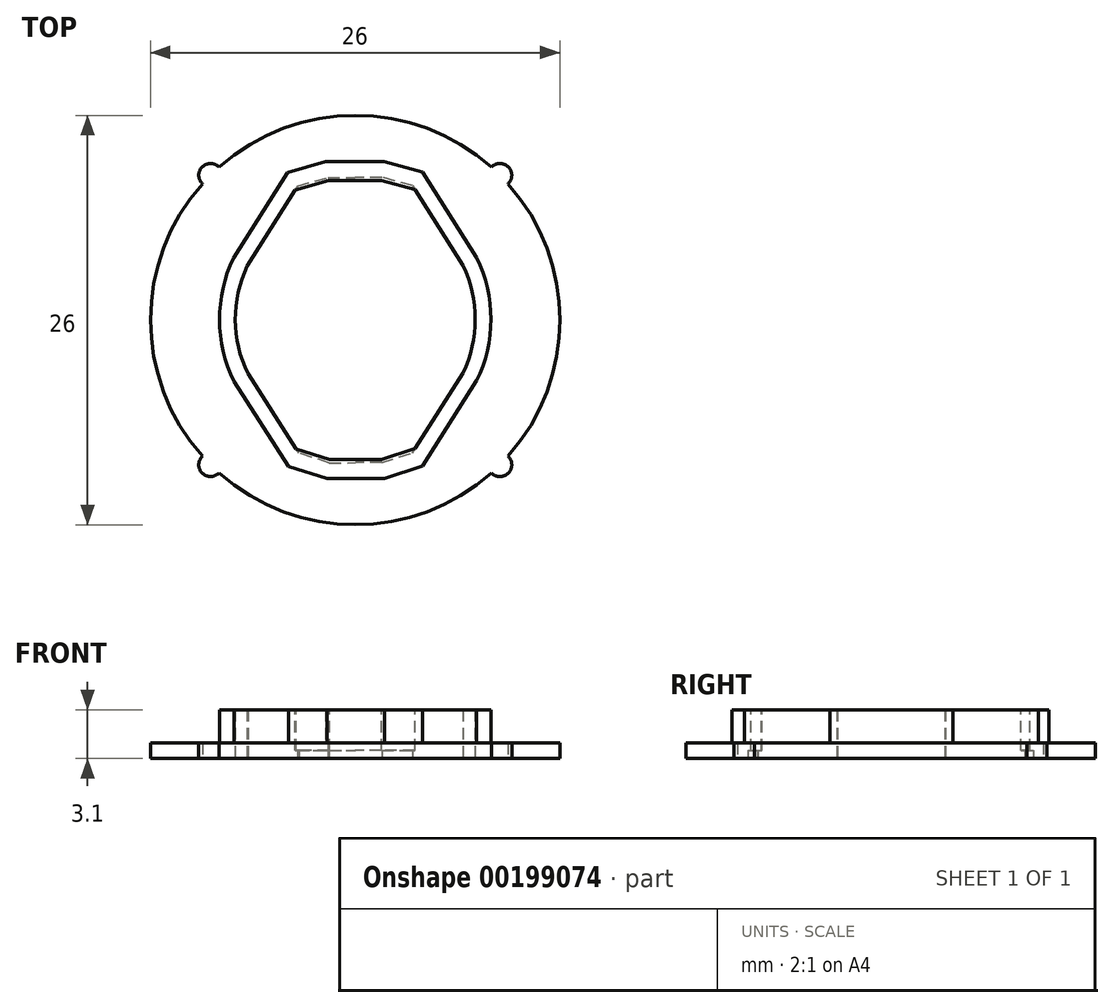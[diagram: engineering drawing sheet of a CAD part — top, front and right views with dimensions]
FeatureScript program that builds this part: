
annotation { "Feature Type Name" : "Feature", "Feature Type Description" : "" }
export const myFeature = defineFeature(function(context is Context, id is Id, definition is map)
    precondition{}
    {
        {
            var Q0;
            Q0=qCreatedBy(makeId("Top.planeOp"),FACE);
            var sketch = newSketch(context, id + "F0", { "sketchPlane" : qUnion([Q0])});
            skLineSegment(sketch, "E0", {"start": v(-52.92, -44.13) * mm, "end": v(-52.88, -62.26) * mm, "construction": true});
            skCircle(sketch, "E1", {"center": v(-52.9, -53.2) * mm, "radius": 13 * mm});
            skLineSegment(sketch, "E2", {"start": v(-49.27, -44.66) * mm, "end": v(-46.06, -49.73) * mm});
            skLineSegment(sketch, "E3", {"start": v(-49.27, -44.66) * mm, "end": v(-51.2, -44.13) * mm});
            skLineSegment(sketch, "E4", {"start": v(-51.2, -44.13) * mm, "end": v(-52.92, -44.13) * mm});
            skLineSegment(sketch, "E5", {"start": v(-52.92, -44.13) * mm, "end": v(-52.88, -62.26) * mm});
            skLineSegment(sketch, "E6", {"start": v(-51.2, -62.26) * mm, "end": v(-49.27, -61.63) * mm});
            skLineSegment(sketch, "E7", {"start": v(-49.27, -61.63) * mm, "end": v(-46.06, -56.57) * mm});
            skArc(sketch, "E8", {"start": v(-46.06, -56.57) * mm, "mid": v(-45.28, -53.15) * mm, "end": v(-46.06, -49.73) * mm});
            skLineSegment(sketch, "E9.MirrorCS", {"start": v(-54.64, -44.14) * mm, "end": v(-52.92, -44.13) * mm});
            skLineSegment(sketch, "E10.MirrorCS", {"start": v(-56.56, -44.68) * mm, "end": v(-54.64, -44.14) * mm});
            skLineSegment(sketch, "E11.MirrorCS", {"start": v(-56.56, -44.68) * mm, "end": v(-59.76, -49.76) * mm});
            skArc(sketch, "E12.MirrorCS", {"start": v(-59.72, -56.6) * mm, "mid": v(-60.52, -53.18) * mm, "end": v(-59.76, -49.76) * mm});
            skLineSegment(sketch, "E13.MirrorCS", {"start": v(-56.48, -61.65) * mm, "end": v(-59.72, -56.6) * mm});
            skLineSegment(sketch, "E14.MirrorCS", {"start": v(-54.55, -62.27) * mm, "end": v(-56.48, -61.65) * mm});
            skLineSegment(sketch, "E15", {"start": v(-54.55, -62.27) * mm, "end": v(-52.88, -62.26) * mm});
            skLineSegment(sketch, "E16", {"start": v(-51.2, -62.26) * mm, "end": v(-52.88, -62.26) * mm});
            skLineSegment(sketch, "E17.0", {"start": v(-48.64, -43.8) * mm, "end": v(-51.07, -43.13) * mm});
            skLineSegment(sketch, "E17.1", {"start": v(-51.07, -43.13) * mm, "end": v(-52.92, -43.13) * mm});
            skLineSegment(sketch, "E17.2", {"start": v(-54.78, -43.14) * mm, "end": v(-52.92, -43.13) * mm});
            skLineSegment(sketch, "E17.3", {"start": v(-51.04, -63.26) * mm, "end": v(-52.87, -63.26) * mm});
            skLineSegment(sketch, "E17.4", {"start": v(-51.04, -63.26) * mm, "end": v(-48.62, -62.47) * mm});
            skLineSegment(sketch, "E17.5", {"start": v(-48.62, -62.47) * mm, "end": v(-45.18, -57.06) * mm});
            skArc(sketch, "E17.6", {"start": v(-45.18, -57.06) * mm, "mid": v(-44.28, -53.15) * mm, "end": v(-45.18, -49.24) * mm});
            skLineSegment(sketch, "E17.7", {"start": v(-54.7, -63.27) * mm, "end": v(-52.87, -63.26) * mm});
            skLineSegment(sketch, "E17.8", {"start": v(-54.7, -63.27) * mm, "end": v(-57.13, -62.5) * mm});
            skLineSegment(sketch, "E17.9", {"start": v(-57.13, -62.5) * mm, "end": v(-60.6, -57.1) * mm});
            skLineSegment(sketch, "E17.10", {"start": v(-48.64, -43.8) * mm, "end": v(-45.18, -49.24) * mm});
            skArc(sketch, "E17.11", {"start": v(-60.6, -57.1) * mm, "mid": v(-61.52, -53.19) * mm, "end": v(-60.63, -49.28) * mm});
            skLineSegment(sketch, "E17.12", {"start": v(-57.2, -43.82) * mm, "end": v(-60.63, -49.28) * mm});
            skLineSegment(sketch, "E17.13", {"start": v(-57.2, -43.82) * mm, "end": v(-54.78, -43.14) * mm});
            skLineSegment(sketch, "E18.bottom", {"start": v(-43.7, -44) * mm, "end": v(-62.1, -44) * mm, "construction": true});
            skLineSegment(sketch, "E18.top", {"start": v(-43.7, -62.4) * mm, "end": v(-62.1, -62.4) * mm, "construction": true});
            skLineSegment(sketch, "E18.left", {"start": v(-43.7, -44) * mm, "end": v(-43.7, -62.4) * mm, "construction": true});
            skLineSegment(sketch, "E18.right", {"start": v(-62.1, -44) * mm, "end": v(-62.1, -62.4) * mm, "construction": true});
            skCircle(sketch, "E19", {"center": v(-43.7, -44) * mm, "radius": 0.5 * mm});
            skCircle(sketch, "E20", {"center": v(-62.1, -44) * mm, "radius": 0.5 * mm});
            skCircle(sketch, "E21", {"center": v(-43.7, -62.4) * mm, "radius": 0.5 * mm});
            skCircle(sketch, "E22", {"center": v(-62.1, -62.4) * mm, "radius": 0.5 * mm});
            skCircle(sketch, "E23", {"center": v(-62.1, -44) * mm, "radius": 0.75 * mm});
            skCircle(sketch, "E24", {"center": v(-43.7, -44) * mm, "radius": 0.75 * mm});
            skCircle(sketch, "E25", {"center": v(-43.7, -62.4) * mm, "radius": 0.75 * mm});
            skCircle(sketch, "E26", {"center": v(-62.1, -62.4) * mm, "radius": 0.75 * mm});
            skSolve(sketch);
        }
        {
            var Q0;
            Q0=makeQuery(id+"F0.imprint","IMPRINT",FACE,{"disambiguationData":[TD([[makeQuery(id+"F0.imprint","IMPRINT",EDGE,{"derivedFrom":sQuery(id+"F0.wireOp",EDGE,"E2")}),1.0]])]});
            var Q1;
            Q1=sQuery(id+"F0.wireOp",EDGE,"E17.11");
            var Q2;
            Q2=sQuery(id+"F0.wireOp",EDGE,"E12.MirrorCS");
            extrude(context, id + "F1", {"entities" : qUnion([Q0]), "surfaceEntities" : qUnion([Q1, Q2]), "depth" : 3.1 * mm});
        }
        {
            var Q0;
            Q0=makeQuery(id+"F1.opExtrude","CAP_FACE",FACE,{"disambiguationData":[OSD([sQuery(id+"F0.wireOp",EDGE,"E2"),sQuery(id+"F0.wireOp",EDGE,"E3"),sQuery(id+"F0.wireOp",EDGE,"E4"),sQuery(id+"F0.wireOp",EDGE,"E6"),sQuery(id+"F0.wireOp",EDGE,"E7"),sQuery(id+"F0.wireOp",EDGE,"E8"),sQuery(id+"F0.wireOp",EDGE,"E9.MirrorCS"),sQuery(id+"F0.wireOp",EDGE,"E10.MirrorCS"),sQuery(id+"F0.wireOp",EDGE,"E11.MirrorCS"),sQuery(id+"F0.wireOp",EDGE,"E12.MirrorCS"),sQuery(id+"F0.wireOp",EDGE,"E13.MirrorCS"),sQuery(id+"F0.wireOp",EDGE,"E14.MirrorCS"),sQuery(id+"F0.wireOp",EDGE,"E15"),sQuery(id+"F0.wireOp",EDGE,"E16"),sQuery(id+"F0.wireOp",EDGE,"E17.0"),sQuery(id+"F0.wireOp",EDGE,"E17.1"),sQuery(id+"F0.wireOp",EDGE,"E17.2"),sQuery(id+"F0.wireOp",EDGE,"E17.3"),sQuery(id+"F0.wireOp",EDGE,"E17.4"),sQuery(id+"F0.wireOp",EDGE,"E17.5"),sQuery(id+"F0.wireOp",EDGE,"E17.6"),sQuery(id+"F0.wireOp",EDGE,"E17.7"),sQuery(id+"F0.wireOp",EDGE,"E17.8"),sQuery(id+"F0.wireOp",EDGE,"E17.9"),sQuery(id+"F0.wireOp",EDGE,"E17.10"),sQuery(id+"F0.wireOp",EDGE,"E17.11"),sQuery(id+"F0.wireOp",EDGE,"E17.12"),sQuery(id+"F0.wireOp",EDGE,"E17.13")])],"isStart":true});
            var sketch = newSketch(context, id + "F2", { "sketchPlane" : qUnion([Q0])});
            skLineSegment(sketch, "E27", {"start": v(-52.92, 44.13) * mm, "end": v(-52.88, 62.26) * mm, "construction": true});
            skCircle(sketch, "E28", {"center": v(-52.9, 53.2) * mm, "radius": 13 * mm});
            skLineSegment(sketch, "E29.bottom", {"start": v(-43.7, 62.4) * mm, "end": v(-62.1, 62.4) * mm, "construction": true});
            skLineSegment(sketch, "E29.top", {"start": v(-43.7, 44) * mm, "end": v(-62.1, 44) * mm, "construction": true});
            skLineSegment(sketch, "E29.left", {"start": v(-43.7, 62.4) * mm, "end": v(-43.7, 44) * mm, "construction": true});
            skLineSegment(sketch, "E29.right", {"start": v(-62.1, 62.4) * mm, "end": v(-62.1, 44) * mm, "construction": true});
            skCircle(sketch, "E30", {"center": v(-43.7, 62.4) * mm, "radius": 0.5 * mm});
            skCircle(sketch, "E31", {"center": v(-62.1, 62.4) * mm, "radius": 0.5 * mm});
            skCircle(sketch, "E32", {"center": v(-43.7, 44) * mm, "radius": 0.5 * mm});
            skCircle(sketch, "E33", {"center": v(-62.1, 44) * mm, "radius": 0.5 * mm});
            skCircle(sketch, "E34", {"center": v(-43.7, 44) * mm, "radius": 0.75 * mm});
            skCircle(sketch, "E35", {"center": v(-62.1, 44) * mm, "radius": 0.75 * mm});
            skCircle(sketch, "E36", {"center": v(-62.1, 62.4) * mm, "radius": 0.75 * mm});
            skCircle(sketch, "E37", {"center": v(-43.7, 62.4) * mm, "radius": 0.75 * mm});
            skSolve(sketch);
        }
        {
            var Q0;
            {var subQ0=sQuery(id+"F2.wireOp",EDGE,"E37");var subQ1=sQuery(id+"F2.wireOp",EDGE,"E28");var subQ2=makeQuery(id+"F2.imprint","INTERSECT",VERTEX,{"disambiguationData":[OD(0.0)],"derivedFrom":[subQ1,subQ0]});Q0=makeQuery(id+"F2.imprint","IMPRINT",FACE,{"disambiguationData":[TD([[makeQuery(id+"F2.imprint","IMPRINT",EDGE,{"disambiguationData":[TD([[subQ2,-1.0]])],"derivedFrom":subQ1}),-1.0]])]});}
            var Q1;
            {var subQ0=sQuery(id+"F2.wireOp",EDGE,"E30");var subQ1=sQuery(id+"F2.wireOp",EDGE,"E28");var subQ2=makeQuery(id+"F2.imprint","INTERSECT",VERTEX,{"disambiguationData":[OD(0.0)],"derivedFrom":[subQ1,subQ0]});Q1=makeQuery(id+"F2.imprint","IMPRINT",FACE,{"disambiguationData":[TD([[makeQuery(id+"F2.imprint","IMPRINT",EDGE,{"disambiguationData":[TD([[subQ2,-1.0]])],"derivedFrom":subQ1}),-1.0]])]});}
            var Q2;
            {var subQ0=sQuery(id+"F2.wireOp",EDGE,"E30");var subQ1=sQuery(id+"F2.wireOp",EDGE,"E28");var subQ2=makeQuery(id+"F2.imprint","INTERSECT",VERTEX,{"disambiguationData":[OD(0.0)],"derivedFrom":[subQ1,subQ0]});Q2=makeQuery(id+"F2.imprint","IMPRINT",FACE,{"disambiguationData":[TD([[makeQuery(id+"F2.imprint","IMPRINT",EDGE,{"disambiguationData":[TD([[subQ2,-1.0]])],"derivedFrom":subQ1}),1.0]])]});}
            var Q3;
            Q3=makeQuery(id+"F2.imprint","IMPRINT",FACE,{"disambiguationData":[TD([[makeQuery(id+"F2.imprint","IMPRINT",EDGE,{"derivedFrom":makeQuery(id+"F1.opExtrude","CAP_EDGE",EDGE,{"disambiguationData":[OSD([sQuery(id+"F0.wireOp",EDGE,"E17.0")])],"isStart":true})}),1.0]])]});
            var Q4;
            {var subQ0=sQuery(id+"F2.wireOp",EDGE,"E37");var subQ1=sQuery(id+"F2.wireOp",EDGE,"E28");var subQ2=makeQuery(id+"F2.imprint","INTERSECT",VERTEX,{"disambiguationData":[OD(0.0)],"derivedFrom":[subQ1,subQ0]});Q4=makeQuery(id+"F2.imprint","IMPRINT",FACE,{"disambiguationData":[TD([[makeQuery(id+"F2.imprint","IMPRINT",EDGE,{"disambiguationData":[TD([[subQ2,-1.0]])],"derivedFrom":subQ1}),1.0]])]});}
            var Q5;
            {var subQ0=sQuery(id+"F2.wireOp",EDGE,"E36");var subQ1=sQuery(id+"F2.wireOp",EDGE,"E28");var subQ2=makeQuery(id+"F2.imprint","INTERSECT",VERTEX,{"disambiguationData":[OD(0.0)],"derivedFrom":[subQ1,subQ0]});Q5=makeQuery(id+"F2.imprint","IMPRINT",FACE,{"disambiguationData":[TD([[makeQuery(id+"F2.imprint","IMPRINT",EDGE,{"disambiguationData":[TD([[subQ2,-1.0]])],"derivedFrom":subQ1}),-1.0]])]});}
            var Q6;
            {var subQ0=sQuery(id+"F2.wireOp",EDGE,"E36");var subQ1=sQuery(id+"F2.wireOp",EDGE,"E28");var subQ2=makeQuery(id+"F2.imprint","INTERSECT",VERTEX,{"disambiguationData":[OD(0.0)],"derivedFrom":[subQ1,subQ0]});Q6=makeQuery(id+"F2.imprint","IMPRINT",FACE,{"disambiguationData":[TD([[makeQuery(id+"F2.imprint","IMPRINT",EDGE,{"disambiguationData":[TD([[subQ2,-1.0]])],"derivedFrom":subQ1}),1.0]])]});}
            var Q7;
            {var subQ0=sQuery(id+"F2.wireOp",EDGE,"E31");var subQ1=sQuery(id+"F2.wireOp",EDGE,"E28");var subQ2=makeQuery(id+"F2.imprint","INTERSECT",VERTEX,{"disambiguationData":[OD(0.0)],"derivedFrom":[subQ1,subQ0]});Q7=makeQuery(id+"F2.imprint","IMPRINT",FACE,{"disambiguationData":[TD([[makeQuery(id+"F2.imprint","IMPRINT",EDGE,{"disambiguationData":[TD([[subQ2,-1.0]])],"derivedFrom":subQ1}),-1.0]])]});}
            var Q8;
            {var subQ0=sQuery(id+"F2.wireOp",EDGE,"E31");var subQ1=sQuery(id+"F2.wireOp",EDGE,"E28");var subQ2=makeQuery(id+"F2.imprint","INTERSECT",VERTEX,{"disambiguationData":[OD(0.0)],"derivedFrom":[subQ1,subQ0]});Q8=makeQuery(id+"F2.imprint","IMPRINT",FACE,{"disambiguationData":[TD([[makeQuery(id+"F2.imprint","IMPRINT",EDGE,{"disambiguationData":[TD([[subQ2,-1.0]])],"derivedFrom":subQ1}),1.0]])]});}
            var Q9;
            {var subQ0=sQuery(id+"F2.wireOp",EDGE,"E34");var subQ1=sQuery(id+"F2.wireOp",EDGE,"E28");var subQ2=makeQuery(id+"F2.imprint","INTERSECT",VERTEX,{"disambiguationData":[OD(0.0)],"derivedFrom":[subQ1,subQ0]});Q9=makeQuery(id+"F2.imprint","IMPRINT",FACE,{"disambiguationData":[TD([[makeQuery(id+"F2.imprint","IMPRINT",EDGE,{"disambiguationData":[TD([[subQ2,-1.0]])],"derivedFrom":subQ1}),-1.0]])]});}
            var Q10;
            {var subQ0=sQuery(id+"F2.wireOp",EDGE,"E32");var subQ1=sQuery(id+"F2.wireOp",EDGE,"E28");var subQ2=makeQuery(id+"F2.imprint","INTERSECT",VERTEX,{"disambiguationData":[OD(0.0)],"derivedFrom":[subQ1,subQ0]});Q10=makeQuery(id+"F2.imprint","IMPRINT",FACE,{"disambiguationData":[TD([[makeQuery(id+"F2.imprint","IMPRINT",EDGE,{"disambiguationData":[TD([[subQ2,-1.0]])],"derivedFrom":subQ1}),-1.0]])]});}
            var Q11;
            {var subQ0=sQuery(id+"F2.wireOp",EDGE,"E32");var subQ1=sQuery(id+"F2.wireOp",EDGE,"E28");var subQ2=makeQuery(id+"F2.imprint","INTERSECT",VERTEX,{"disambiguationData":[OD(0.0)],"derivedFrom":[subQ1,subQ0]});Q11=makeQuery(id+"F2.imprint","IMPRINT",FACE,{"disambiguationData":[TD([[makeQuery(id+"F2.imprint","IMPRINT",EDGE,{"disambiguationData":[TD([[subQ2,-1.0]])],"derivedFrom":subQ1}),1.0]])]});}
            var Q12;
            {var subQ0=sQuery(id+"F2.wireOp",EDGE,"E34");var subQ1=sQuery(id+"F2.wireOp",EDGE,"E28");var subQ2=makeQuery(id+"F2.imprint","INTERSECT",VERTEX,{"disambiguationData":[OD(0.0)],"derivedFrom":[subQ1,subQ0]});Q12=makeQuery(id+"F2.imprint","IMPRINT",FACE,{"disambiguationData":[TD([[makeQuery(id+"F2.imprint","IMPRINT",EDGE,{"disambiguationData":[TD([[subQ2,-1.0]])],"derivedFrom":subQ1}),1.0]])]});}
            var Q13;
            {var subQ0=sQuery(id+"F2.wireOp",EDGE,"E35");var subQ1=sQuery(id+"F2.wireOp",EDGE,"E28");var subQ2=makeQuery(id+"F2.imprint","INTERSECT",VERTEX,{"disambiguationData":[OD(0.0)],"derivedFrom":[subQ1,subQ0]});Q13=makeQuery(id+"F2.imprint","IMPRINT",FACE,{"disambiguationData":[TD([[makeQuery(id+"F2.imprint","IMPRINT",EDGE,{"disambiguationData":[TD([[subQ2,-1.0]])],"derivedFrom":subQ1}),-1.0]])]});}
            var Q14;
            {var subQ0=sQuery(id+"F2.wireOp",EDGE,"E33");var subQ1=sQuery(id+"F2.wireOp",EDGE,"E28");var subQ2=makeQuery(id+"F2.imprint","INTERSECT",VERTEX,{"disambiguationData":[OD(0.0)],"derivedFrom":[subQ1,subQ0]});Q14=makeQuery(id+"F2.imprint","IMPRINT",FACE,{"disambiguationData":[TD([[makeQuery(id+"F2.imprint","IMPRINT",EDGE,{"disambiguationData":[TD([[subQ2,-1.0]])],"derivedFrom":subQ1}),-1.0]])]});}
            var Q15;
            {var subQ0=sQuery(id+"F2.wireOp",EDGE,"E33");var subQ1=sQuery(id+"F2.wireOp",EDGE,"E28");var subQ2=makeQuery(id+"F2.imprint","INTERSECT",VERTEX,{"disambiguationData":[OD(0.0)],"derivedFrom":[subQ1,subQ0]});Q15=makeQuery(id+"F2.imprint","IMPRINT",FACE,{"disambiguationData":[TD([[makeQuery(id+"F2.imprint","IMPRINT",EDGE,{"disambiguationData":[TD([[subQ2,-1.0]])],"derivedFrom":subQ1}),1.0]])]});}
            var Q16;
            {var subQ0=sQuery(id+"F2.wireOp",EDGE,"E35");var subQ1=sQuery(id+"F2.wireOp",EDGE,"E28");var subQ2=makeQuery(id+"F2.imprint","INTERSECT",VERTEX,{"disambiguationData":[OD(0.0)],"derivedFrom":[subQ1,subQ0]});Q16=makeQuery(id+"F2.imprint","IMPRINT",FACE,{"disambiguationData":[TD([[makeQuery(id+"F2.imprint","IMPRINT",EDGE,{"disambiguationData":[TD([[subQ2,-1.0]])],"derivedFrom":subQ1}),1.0]])]});}
            extrude(context, id + "F3", {"entities" : qUnion([Q0, Q1, Q2, Q3, Q4, Q5, Q6, Q7, Q8, Q9, Q10, Q11, Q12, Q13, Q14, Q15, Q16]), "operationType" : NewBodyOperationType.ADD, "oppositeDirection" : true, "depth" : 1 * mm});
        }
        {
            var Q0;
            {var subQ0=sQuery(id+"F0.wireOp",EDGE,"E17.13");var subQ1=sQuery(id+"F0.wireOp",EDGE,"E17.12");var subQ2=sQuery(id+"F0.wireOp",EDGE,"E17.11");var subQ3=sQuery(id+"F0.wireOp",EDGE,"E17.10");var subQ4=sQuery(id+"F0.wireOp",EDGE,"E17.9");var subQ5=sQuery(id+"F0.wireOp",EDGE,"E17.8");var subQ6=sQuery(id+"F0.wireOp",EDGE,"E17.7");var subQ7=sQuery(id+"F0.wireOp",EDGE,"E17.6");var subQ8=sQuery(id+"F0.wireOp",EDGE,"E17.5");var subQ9=sQuery(id+"F0.wireOp",EDGE,"E17.4");var subQ10=sQuery(id+"F0.wireOp",EDGE,"E17.3");var subQ11=sQuery(id+"F0.wireOp",EDGE,"E17.2");var subQ12=sQuery(id+"F0.wireOp",EDGE,"E17.1");var subQ13=sQuery(id+"F0.wireOp",EDGE,"E17.0");Q0=makeQuery(id+"F3.boolean.opBoolean","MERGE",FACE,{"derivedFrom":[makeQuery(id+"F1.opExtrude","CAP_FACE",FACE,{"disambiguationData":[OSD([sQuery(id+"F0.wireOp",EDGE,"E2"),sQuery(id+"F0.wireOp",EDGE,"E3"),sQuery(id+"F0.wireOp",EDGE,"E4"),sQuery(id+"F0.wireOp",EDGE,"E6"),sQuery(id+"F0.wireOp",EDGE,"E7"),sQuery(id+"F0.wireOp",EDGE,"E8"),sQuery(id+"F0.wireOp",EDGE,"E9.MirrorCS"),sQuery(id+"F0.wireOp",EDGE,"E10.MirrorCS"),sQuery(id+"F0.wireOp",EDGE,"E11.MirrorCS"),sQuery(id+"F0.wireOp",EDGE,"E12.MirrorCS"),sQuery(id+"F0.wireOp",EDGE,"E13.MirrorCS"),sQuery(id+"F0.wireOp",EDGE,"E14.MirrorCS"),sQuery(id+"F0.wireOp",EDGE,"E15"),sQuery(id+"F0.wireOp",EDGE,"E16"),subQ13,subQ12,subQ11,subQ10,subQ9,subQ8,subQ7,subQ6,subQ5,subQ4,subQ3,subQ2,subQ1,subQ0])],"isStart":true}),makeQuery(id+"F3.opExtrude","CAP_FACE",FACE,{"disambiguationData":[OSD([subQ13,subQ12,subQ11,subQ10,subQ9,subQ8,subQ7,subQ6,subQ5,subQ4,subQ3,subQ2,subQ1,subQ0,sQuery(id+"F2.wireOp",EDGE,"E28"),sQuery(id+"F2.wireOp",EDGE,"E30"),sQuery(id+"F2.wireOp",EDGE,"E31"),sQuery(id+"F2.wireOp",EDGE,"E32"),sQuery(id+"F2.wireOp",EDGE,"E33")])],"isStart":true})]});}
            var sketch = newSketch(context, id + "F4", { "sketchPlane" : qUnion([Q0])});
            skLineSegment(sketch, "E38", {"start": v(-60.52, 53.1) * mm, "end": v(-65.9, 53.1) * mm, "construction": true});
            skPoint(sketch, "E38.startSnap0", {"position": v(-60.52, 53.18) * mm});
            skLineSegment(sketch, "E39.bottom", {"start": v(-66.78, 54.4) * mm, "end": v(-54.25, 54.4) * mm});
            skLineSegment(sketch, "E39.top", {"start": v(-66.78, 51.82) * mm, "end": v(-54.25, 51.82) * mm});
            skLineSegment(sketch, "E39.left", {"start": v(-66.78, 54.4) * mm, "end": v(-66.78, 51.82) * mm});
            skLineSegment(sketch, "E39.right", {"start": v(-54.25, 54.4) * mm, "end": v(-54.25, 51.82) * mm});
            skPoint(sketch, "E39.middle", {"position": v(-60.52, 53.1) * mm});
            skSolve(sketch);
        }
        {
            var Q0;
            {var subQ0=sQuery(id+"F4.wireOp",EDGE,"E39.bottom");var subQ4=makeQuery(id+"F1.opExtrude","CAP_EDGE",EDGE,{"disambiguationData":[OSD([sQuery(id+"F0.wireOp",EDGE,"E12.MirrorCS")])],"isStart":true});var subQ5=makeQuery(id+"F4.imprint","INTERSECT",VERTEX,{"derivedFrom":[subQ4,subQ0]});Q0=makeQuery(id+"F4.imprint","IMPRINT",FACE,{"disambiguationData":[TD([[makeQuery(id+"F4.imprint","IMPRINT",EDGE,{"disambiguationData":[TD([[subQ5,-1.0]])],"derivedFrom":subQ4}),-1.0]])]});}
            extrude(context, id + "F5", {"entities" : qUnion([Q0]), "operationType" : NewBodyOperationType.REMOVE, "oppositeDirection" : true, "depth" : 3.1 * mm});
        }
        {
            var Q0;
            Q0=makeQuery(id+"F1.opExtrude","CAP_FACE",FACE,{"disambiguationData":[OSD([sQuery(id+"F0.wireOp",EDGE,"E2"),sQuery(id+"F0.wireOp",EDGE,"E3"),sQuery(id+"F0.wireOp",EDGE,"E4"),sQuery(id+"F0.wireOp",EDGE,"E6"),sQuery(id+"F0.wireOp",EDGE,"E7"),sQuery(id+"F0.wireOp",EDGE,"E8"),sQuery(id+"F0.wireOp",EDGE,"E9.MirrorCS"),sQuery(id+"F0.wireOp",EDGE,"E10.MirrorCS"),sQuery(id+"F0.wireOp",EDGE,"E11.MirrorCS"),sQuery(id+"F0.wireOp",EDGE,"E12.MirrorCS"),sQuery(id+"F0.wireOp",EDGE,"E13.MirrorCS"),sQuery(id+"F0.wireOp",EDGE,"E14.MirrorCS"),sQuery(id+"F0.wireOp",EDGE,"E15"),sQuery(id+"F0.wireOp",EDGE,"E16"),sQuery(id+"F0.wireOp",EDGE,"E17.0"),sQuery(id+"F0.wireOp",EDGE,"E17.1"),sQuery(id+"F0.wireOp",EDGE,"E17.2"),sQuery(id+"F0.wireOp",EDGE,"E17.3"),sQuery(id+"F0.wireOp",EDGE,"E17.4"),sQuery(id+"F0.wireOp",EDGE,"E17.5"),sQuery(id+"F0.wireOp",EDGE,"E17.6"),sQuery(id+"F0.wireOp",EDGE,"E17.7"),sQuery(id+"F0.wireOp",EDGE,"E17.8"),sQuery(id+"F0.wireOp",EDGE,"E17.9"),sQuery(id+"F0.wireOp",EDGE,"E17.10"),sQuery(id+"F0.wireOp",EDGE,"E17.11"),sQuery(id+"F0.wireOp",EDGE,"E17.12"),sQuery(id+"F0.wireOp",EDGE,"E17.13")])],"isStart":false});
            var sketch = newSketch(context, id + "F6", { "sketchPlane" : qUnion([Q0])});
            skLineSegment(sketch, "E40.0", {"start": v(-56.72, -44.93) * mm, "end": v(-54.58, -44.33) * mm});
            skLineSegment(sketch, "E41.0", {"start": v(-54.64, -44.34) * mm, "end": v(-52.92, -44.33) * mm});
            skLineSegment(sketch, "E42.0", {"start": v(-51.2, -44.33) * mm, "end": v(-52.92, -44.33) * mm});
            skLineSegment(sketch, "E43.0", {"start": v(-49.11, -44.91) * mm, "end": v(-51.26, -44.33) * mm});
            skLineSegment(sketch, "E44.0", {"start": v(-54.52, -62.07) * mm, "end": v(-56.65, -61.39) * mm});
            skLineSegment(sketch, "E44.1", {"start": v(-54.52, -62.07) * mm, "end": v(-52.88, -62.06) * mm});
            skLineSegment(sketch, "E44.2", {"start": v(-51.24, -62.06) * mm, "end": v(-52.88, -62.06) * mm});
            skLineSegment(sketch, "E44.3", {"start": v(-51.24, -62.06) * mm, "end": v(-49.1, -61.37) * mm});
            skSolve(sketch);
        }
        {
            var Q0;
            {var subQ11=makeQuery(id+"F1.opExtrude","CAP_EDGE",EDGE,{"disambiguationData":[OSD([sQuery(id+"F0.wireOp",EDGE,"E3")])],"isStart":false});Q0=makeQuery(id+"F6.imprint","IMPRINT",FACE,{"disambiguationData":[TD([[makeQuery(id+"F6.imprint","IMPRINT",EDGE,{"derivedFrom":subQ11}),1.0]])]});}
            var Q1;
            {var subQ5=sQuery(id+"F6.wireOp",EDGE,"E44.0");Q1=makeQuery(id+"F6.imprint","IMPRINT",FACE,{"disambiguationData":[TD([[makeQuery(id+"F6.imprint","IMPRINT",EDGE,{"derivedFrom":subQ5}),1.0]])]});}
            extrude(context, id + "F7", {"entities" : qUnion([Q0, Q1]), "operationType" : NewBodyOperationType.ADD, "oppositeDirection" : true, "depth" : 2.6 * mm});
        }
    });
